# Revit family: Water_Refill_Station-Sensor_Operated-Murdock-SpringH2O-BF168S_Series
name_source: partatom
category: Plumbing Fixtures
units: mm (PartAtom-declared; Revit-internal decimal feet)

## family parameters
Cut with Voids When Loaded = No
Host = Face
OmniClass Number = 23.65.70.14.11
OmniClass Title = Drinking Fountains/Coolers
Part Type = Normal
Room Calculation Point = No
Round Connector Dimension = Use Radius
Shared = Yes

## types (3) — shared parameters
-220V = 220 volt/50 Hz or 60Hz Compressor(CE complaint) = No
-AP = Auto-Purge Function Controller = No
-LOGO Customer Specified Logo / Graphics = No
-WF3 3000-gallon capacity, NSF 42+53, 1 micron Lead Reduction Water Filters = No
ADA Compliant = Yes
Activation By = Sensor (on Bottle Filler)
Assembly Code = D2010800
Bottle Filler Discharge Height = 51 1/4"
Bottle Filler Width = 8 1/8"
CW Connection = Yes
CWFU = 1.5
Cold Water Connection Diameter = 3/8"
Cold Water Connection Height = 30"
Cold Water Connection Radius = 3/16"
Cold Water Connection Width = 6 1/4"
Compliance Certifications = Lead-Free Federal Law 111-380, UPC, UL Listed (US and Canada), CE complaint for 220 V electrical, NSF/ANSI/CAN 61, ANSI/ASHRAE 18
Default Elevation = 0"
Description = Wall-Mounted, SpringH2O® Touchless All-Stainless Steel Water Bottle Filling Station - In-Wall Refrigeration (8 GPH), ADA, Standalone
Fill Rate = 1.2 gallon (4.54 liters) per minute laminar flow nozzle
Full Load Amps = 5 A
HW Connection = No
Height = 52 7/8"
Installation Instruction Link = https://morrisgroup.box.com
Installation Type = Wall Mounted
Length = 23 3/4"
Manufacturer = Murdock Mfg.
Maximum Run Time = 20 Seconds
Mounting Height = 57 5/8"
Power = 120V AC/9V DC plug-in transformer
Product Documentation Link = https://www.murdockmfg.com
Product Page URL = https://www.murdockmfg.com
Rated Watts = 390
Refrigerant Width = 10 7/8"
Sensor Height = 44 1/8"
Shipping Weight = 80 lbs.
Type Comments = Hands-Free Operation
URL = https://www.murdockmfg.com
Vent Connection = No
WFU = 2
Waste Connection = Yes
Waste Connection Diameter = 1 1/4"
Waste Connection Height = 33"
Waste Connection Radius = 5/8"
Waste Connection Width = 3 1/2"
Water Deliver Rate = 8.0 gallons (30.3 liters) per hour of water at 50°F (10°C) cooled from 80°F (26.7°C) inlet water and 90°F (32.2°C) ambient.
Width = 19"
cUPC Compliant = Yes
zero-valued in all types: HWFU

## per-type parameters (varying)
| type | -BCD Bottle Counter Display | -EG Enviro-Glaze® Powder Coating | Bottle Filler Family Type | Finish | Material |
| BF168S | No | No | Bottle_Filler-Murdock-H2O-To-Go-BF16S : BF16S | Stainless Steel-Murdock-Satin | Stainless Steel-Murdock-Satin |
| BF168S-BCD | Yes | No | Bottle_Filler-Murdock-H2O-To-Go-BF16S : BF16S-BCD | Stainless Steel-Murdock-Satin | Stainless Steel-Murdock-Satin |
| BF168S-BCD-EG22 | Yes | Yes | Bottle_Filler-Murdock-H2O-To-Go-BF16S : BF16S-BCD | Stainless Steel-Murdock-Matte Black Powder Coated | Stainless Steel-Murdock-Matte Black Powder Coated |

note: column(s) folded — value = type name in every type: Model

## geometry (parser evidence)
native form markers: Sweep x5
no freeform markers — native parametric forms only
